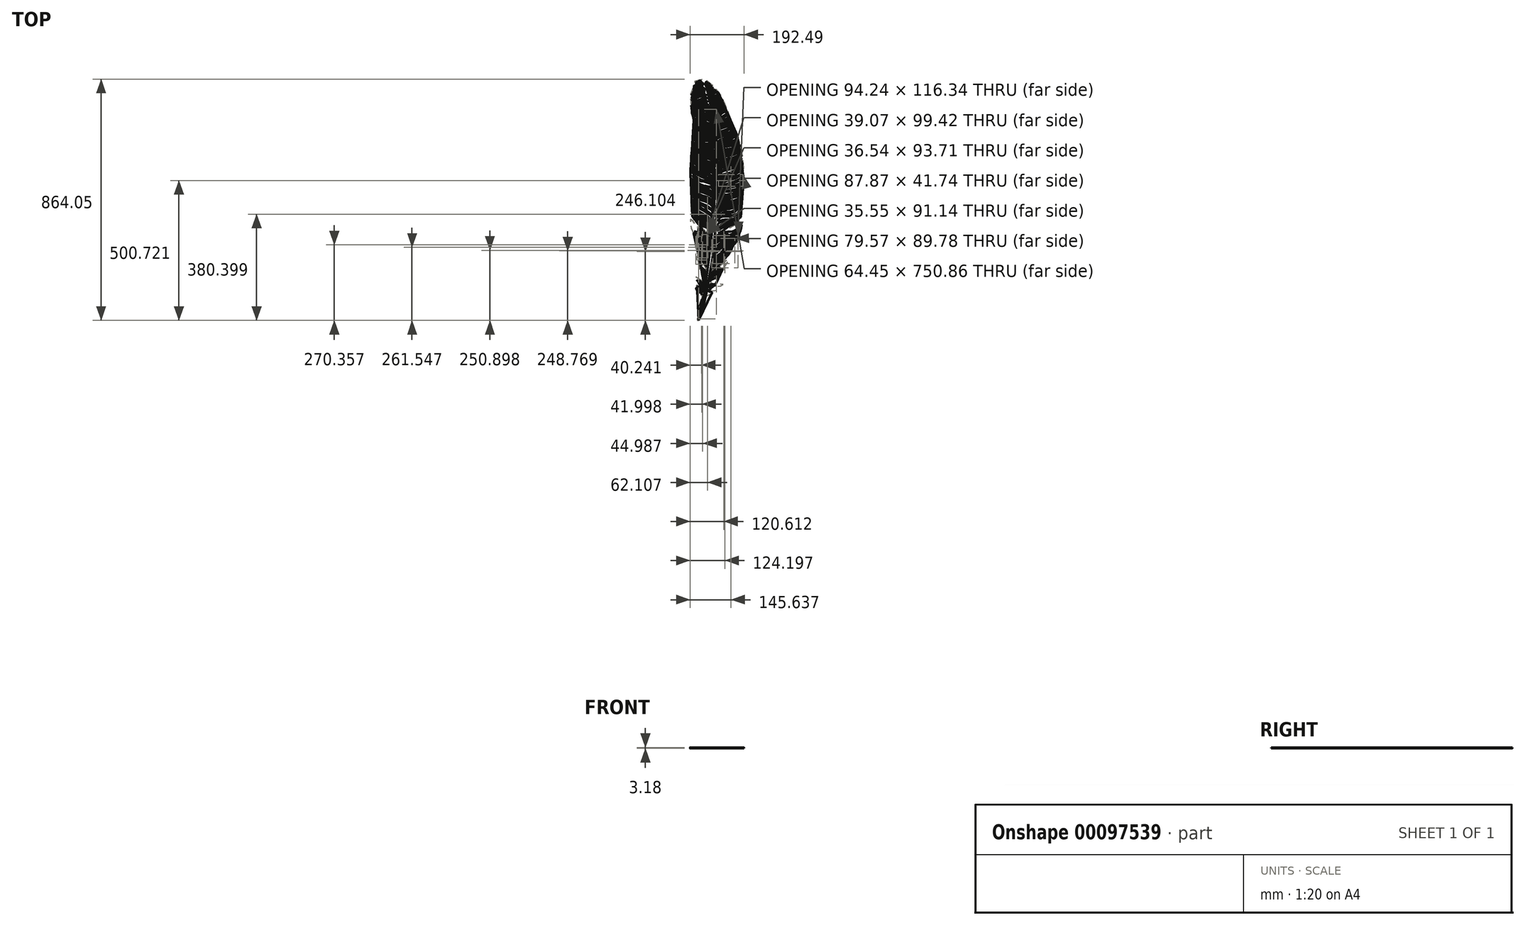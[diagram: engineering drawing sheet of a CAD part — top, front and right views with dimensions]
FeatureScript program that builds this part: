
annotation { "Feature Type Name" : "Feature", "Feature Type Description" : "" }
export const myFeature = defineFeature(function(context is Context, id is Id, definition is map)
    precondition{}
    {
        {
            var Q0;
            Q0=qCreatedBy(makeId("Top.planeOp"),FACE);
            var sketch = newSketch(context, id + "F0", { "sketchPlane" : qUnion([Q0])});
            skFitSpline(sketch, "E0", {"points": [v(-284.28, -414.74) * mm, v(-284.5, -404.7) * mm, v(-276.38, -375.66) * mm, v(-262.7, -314.79) * mm, v(-252.45, -245.37) * mm, v(-244.12, -173.4) * mm, v(-236.65, -109.74) * mm, v(-228.46, -20.33) * mm, v(-226.04, 99.02) * mm, v(-232.9, 203.45) * mm, v(-243.38, 304.25) * mm, v(-248.62, 349.81) * mm, v(-248.05, 351.8) * mm, v(-246.74, 348.7) * mm, v(-237.03, 303.26) * mm, v(-225.9, 221.44) * mm, v(-215.35, 72.9) * mm, v(-225.05, -107.86) * mm, v(-239.82, -235.78) * mm, v(-250.5, -289.17) * mm, v(-258.62, -340) * mm, v(-273.14, -389.13) * mm, v(-284.28, -414.74) * mm]});
            skFitSpline(sketch, "E1", {"points": [v(-284.28, -419.65) * mm, v(-282.38, -419.38) * mm, v(-274.71, -403.64) * mm, v(-261.46, -362.74) * mm, v(-255.63, -337.14) * mm, v(-254.22, -332.65) * mm, v(-249.64, -327.81) * mm, v(-238.34, -325.66) * mm, v(-232.96, -321.9) * mm, v(-241.03, -319.2) * mm, v(-250.18, -324.58) * mm, v(-251.26, -322.16) * mm, v(-246.74, -318.28) * mm, v(-242.56, -315.93) * mm, v(-229, -314.79) * mm, v(-220.02, -311.98) * mm, v(-223.55, -310.8) * mm, v(-240.85, -311.34) * mm, v(-248.54, -313.58) * mm, v(-249.4, -315.82) * mm, v(-250.25, -313.36) * mm, v(-246.74, -308.56) * mm, v(-243.63, -304.71) * mm, v(-234.44, -300.55) * mm, v(-221.41, -297.14) * mm, v(-216.4, -296.18) * mm, v(-189.8, -293.83) * mm, v(-190.55, -291.8) * mm, v(-196.32, -291.48) * mm, v(-219.28, -291.16) * mm, v(-225.9, -287.84) * mm, v(-230.8, -286.67) * mm, v(-241.06, -287.63) * mm, v(-243.73, -286.99) * mm, v(-242.66, -283.36) * mm, v(-232.73, -275.88) * mm, v(-227.07, -272.79) * mm, v(-222.7, -271.08) * mm, v(-213.62, -262.75) * mm, v(-201.65, -243.96) * mm, v(-193.54, -227.83) * mm, v(-177.73, -206.58) * mm, v(-177.3, -201.56) * mm, v(-176.99, -198.9) * mm, v(-179.87, -200.39) * mm, v(-181.26, -203.7) * mm, v(-192.58, -212.13) * mm, v(-197.28, -218.75) * mm, v(-207.2, -225.8) * mm, v(-221.95, -234.87) * mm, v(-233.8, -241.7) * mm, v(-238.82, -245.23) * mm, v(-237.64, -240.53) * mm, v(-231.24, -231.78) * mm, v(-222.8, -221.95) * mm, v(-212.23, -212.02) * mm, v(-199.41, -201.56) * mm, v(-190.01, -194.72) * mm, v(-179.98, -187.04) * mm, v(-171.65, -176.25) * mm, v(-166.2, -165.68) * mm, v(-154.67, -149.24) * mm, v(-151.03, -145.18) * mm, v(-143.88, -134.6) * mm, v(-138.33, -120.4) * mm, v(-138.75, -112.93) * mm, v(-136.4, -104.13) * mm, v(-134.48, -97.9) * mm, v(-132.08, -91.17) * mm, v(-130.48, -78.05) * mm, v(-134.32, -72.93) * mm, v(-140.08, -82.69) * mm, v(-147.28, -93.89) * mm, v(-161.53, -100.93) * mm, v(-185.05, -103) * mm, v(-204.89, -103.8) * mm, v(-213.37, -107.32) * mm, v(-211.6, -103.8) * mm, v(-200.73, -96.28) * mm, v(-180.57, -89.56) * mm, v(-172.89, -87.64) * mm, v(-165.05, -84.92) * mm, v(-144.72, -71.8) * mm, v(-132.72, -48.13) * mm, v(-130.64, -29.73) * mm, v(-128.72, -9.25) * mm, v(-127.92, 9.8) * mm, v(-127.12, 32.2) * mm, v(-123.76, 58.28) * mm, v(-121.68, 85.16) * mm, v(-122.32, 108.04) * mm, v(-123.28, 142.6) * mm, v(-126.48, 170.6) * mm, v(-130.48, 189.49) * mm, v(-137.68, 220.21) * mm, v(-148.73, 251.1) * mm, v(-164.73, 294.14) * mm, v(-180.25, 331.59) * mm, v(-195.13, 368.23) * mm, v(-200.4, 382.31) * mm, v(-214.49, 398.32) * mm, v(-238.97, 428.88) * mm, v(-252.73, 437.85) * mm, v(-264.1, 438.8) * mm, v(-267.77, 439.29) * mm, v(-270.5, 443.45) * mm, v(-288.74, 441.21) * mm, v(-298.82, 433.21) * mm, v(-300.9, 420.25) * mm, v(-305.22, 409.53) * mm, v(-312.73, 392.87) * mm, v(-313, 365.15) * mm, v(-308.96, 343.89) * mm, v(-308.15, 328.28) * mm, v(-306, 317.51) * mm, v(-300.62, 294.1) * mm, v(-299.81, 248.62) * mm, v(-305.73, 203.95) * mm, v(-309.77, 176.77) * mm, v(-311.38, 140.71) * mm, v(-311.38, 82.85) * mm, v(-308.96, 75.05) * mm, v(-311.92, 63.75) * mm, v(-310.85, 13.7) * mm, v(-311.92, -12.4) * mm, v(-310.04, -33.13) * mm, v(-299.27, -61.66) * mm, v(-276.38, -82.92) * mm, v(-246.74, -99.88) * mm, v(-240.6, -105) * mm, v(-238.38, -108.02) * mm, v(-240.08, -110.73) * mm, v(-245.85, -105.41) * mm, v(-266.67, -94.55) * mm, v(-284.28, -88.2) * mm, v(-298.46, -77.46) * mm, v(-304.23, -63.31) * mm, v(-308.76, -57.43) * mm, v(-313.17, -54.94) * mm, v(-312.38, -60.14) * mm, v(-311.13, -85.94) * mm, v(-304.23, -102.91) * mm, v(-294.84, -130.86) * mm, v(-290.31, -178.04) * mm, v(-256.14, -231) * mm, v(-256.03, -234.85) * mm, v(-257.27, -238.36) * mm, v(-274.59, -218.44) * mm, v(-286.13, -197.05) * mm, v(-288.95, -195.92) * mm, v(-288.05, -198.52) * mm, v(-285.45, -211.88) * mm, v(-274.59, -255.9) * mm, v(-265.3, -276.71) * mm, v(-261.12, -280.9) * mm, v(-262.7, -290.63) * mm, v(-266.78, -283.84) * mm, v(-280.8, -273.2) * mm, v(-295.3, -262.68) * mm, v(-297.21, -262.68) * mm, v(-296.88, -265.17) * mm, v(-293.48, -272.75) * mm, v(-287.14, -278.18) * mm, v(-277.41, -297.42) * mm, v(-266.67, -308.5) * mm, v(-266.78, -312.47) * mm, v(-268.93, -314.79) * mm, v(-280.7, -302.73) * mm, v(-288.95, -295.94) * mm, v(-283.07, -308.96) * mm, v(-270.85, -319.14) * mm, v(-272.32, -320.16) * mm, v(-288.5, -307.03) * mm, v(-292.35, -302.84) * mm, v(-291.9, -310.09) * mm, v(-284.28, -315.63) * mm, v(-275.5, -321.85) * mm, v(-272.1, -328.76) * mm, v(-272.32, -342.1) * mm, v(-281.94, -377.75) * mm, v(-288.05, -402.75) * mm, v(-288.28, -417) * mm, v(-287.37, -419.5) * mm, v(-284.28, -419.65) * mm]});
            skFitSpline(sketch, "E2", {"points": [v(-283.14, 436.73) * mm, v(-280.72, 434.91) * mm, v(-274.71, 435.72) * mm, v(-277.5, 438.74) * mm, v(-281.93, 439.15) * mm, v(-283.14, 436.73) * mm]});
            skFitSpline(sketch, "E3", {"points": [v(-266.2, 424.83) * mm, v(-270.04, 426.04) * mm, v(-279.1, 425.84) * mm, v(-291, 426.04) * mm, v(-292.82, 430.28) * mm, v(-290.8, 431.69) * mm, v(-291.2, 434.5) * mm, v(-288.58, 433.1) * mm, v(-281.93, 431.48) * mm, v(-271.85, 431.08) * mm, v(-266.2, 428.05) * mm, v(-266.2, 424.83) * mm]});
            skFitSpline(sketch, "E4", {"points": [v(-266.58, 419.95) * mm, v(-272.15, 418.87) * mm, v(-282.92, 416.54) * mm, v(-285.08, 415.1) * mm, v(-292.98, 415.64) * mm, v(-296.4, 420.31) * mm, v(-296.75, 422.3) * mm, v(-293.16, 421.21) * mm, v(-286.7, 421.93) * mm, v(-279.69, 421.75) * mm, v(-272.86, 422.65) * mm, v(-269.81, 420.31) * mm, v(-266.58, 419.95) * mm]});
            skFitSpline(sketch, "E5", {"points": [v(-257.2, 434.22) * mm, v(-258.33, 429.92) * mm, v(-261.95, 425.4) * mm, v(-260.14, 424.49) * mm, v(-256.74, 428.56) * mm, v(-252.9, 431.28) * mm, v(-254.03, 434) * mm, v(-257.2, 434.22) * mm]});
            skFitSpline(sketch, "E6", {"points": [v(-257.42, 418.6) * mm, v(-255.16, 423.8) * mm, v(-248.37, 429.47) * mm, v(-246.33, 428.79) * mm, v(-243.85, 425.4) * mm, v(-247.47, 424.49) * mm, v(-256.07, 415.66) * mm, v(-257.42, 418.6) * mm]});
            skFitSpline(sketch, "E7", {"points": [v(-266.7, 413.85) * mm, v(-273.49, 412.05) * mm, v(-280.73, 408.65) * mm, v(-291.14, 407.07) * mm, v(-302.23, 405.94) * mm, v(-300.87, 409.79) * mm, v(-296.8, 412.5) * mm, v(-291.82, 410.01) * mm, v(-280.73, 412.05) * mm, v(-273.04, 414.53) * mm, v(-266.7, 413.85) * mm]});
            skFitSpline(sketch, "E8", {"points": [v(-237.5, 417.47) * mm, v(-241.13, 416.34) * mm, v(-247.47, 410.46) * mm, v(-253.8, 405.93) * mm, v(-256.74, 405.25) * mm, v(-254.7, 409.33) * mm, v(-249.28, 415.89) * mm, v(-244.98, 419.5) * mm, v(-238.64, 419.96) * mm, v(-237.5, 417.47) * mm]});
            skFitSpline(sketch, "E9", {"points": [v(-262.85, 406.84) * mm, v(-263.76, 405.03) * mm, v(-271.45, 403.45) * mm, v(-281.18, 401.86) * mm, v(-289.33, 400.5) * mm, v(-297.25, 396.2) * mm, v(-304.5, 397.12) * mm, v(-300.64, 400.5) * mm, v(-291.14, 402.54) * mm, v(-278.02, 405.7) * mm, v(-270.32, 409.1) * mm, v(-263.99, 409.78) * mm, v(-262.85, 406.84) * mm]});
            skFitSpline(sketch, "E10", {"points": [v(-260.6, 397.79) * mm, v(-262.63, 400.73) * mm, v(-273.72, 399.37) * mm, v(-286.61, 396.2) * mm, v(-293.63, 393.95) * mm, v(-305.62, 390.78) * mm, v(-309.02, 390.55) * mm, v(-308.34, 386.48) * mm, v(-300.64, 387.84) * mm, v(-286.39, 392.81) * mm, v(-273.26, 397.34) * mm, v(-260.6, 397.79) * mm]});
            skFitSpline(sketch, "E11", {"points": [v(-182.7, -107.46) * mm, v(-201.65, -107.7) * mm, v(-214.49, -112.97) * mm, v(-221.95, -122.32) * mm, v(-221.95, -129.27) * mm, v(-219.62, -125.67) * mm, v(-207.2, -117.52) * mm, v(-190.61, -111.77) * mm, v(-182.7, -107.46) * mm]});
            skFitSpline(sketch, "E12", {"points": [v(-221.78, -141.74) * mm, v(-223.94, -145.1) * mm, v(-225.37, -142.22) * mm, v(-223.7, -135.26) * mm, v(-213.39, -126.15) * mm, v(-193.97, -117.53) * mm, v(-177.9, -111.06) * mm, v(-198.52, -122.32) * mm, v(-216.98, -136.94) * mm, v(-221.78, -141.74) * mm]});
            skFitSpline(sketch, "E13", {"points": [v(-264.68, -304.71) * mm, v(-271.8, -297.42) * mm, v(-279.34, -283.64) * mm, v(-281.63, -278.26) * mm, v(-279.88, -278.12) * mm, v(-273.15, -285.26) * mm, v(-267.23, -294) * mm, v(-263.74, -297.42) * mm, v(-264.68, -300.06) * mm, v(-264.68, -304.71) * mm]});
            skFitSpline(sketch, "E14", {"points": [v(-223.5, -293.07) * mm, v(-230.64, -290.78) * mm, v(-239.92, -290.64) * mm, v(-245.57, -293.6) * mm, v(-246.92, -296.3) * mm, v(-248.4, -300.73) * mm, v(-242.07, -298.45) * mm, v(-234.27, -296.56) * mm, v(-226.6, -294.41) * mm, v(-223.5, -293.07) * mm]});
            skFitSpline(sketch, "E15", {"points": [v(-205.8, -244.3) * mm, v(-215.65, -252.7) * mm, v(-226.62, -259.68) * mm, v(-235.75, -266.1) * mm, v(-242.66, -273.22) * mm, v(-244.58, -278.36) * mm, v(-237.17, -274.37) * mm, v(-225.77, -268.1) * mm, v(-213.8, -256.55) * mm, v(-205.8, -244.3) * mm]});
            skFitSpline(sketch, "E16", {"points": [v(-258.7, -269.09) * mm, v(-258.13, -275.08) * mm, v(-261.7, -272.65) * mm, v(-265.11, -265.52) * mm, v(-266.97, -260.4) * mm, v(-262.26, -264.67) * mm, v(-258.7, -269.09) * mm]});
            skFitSpline(sketch, "E17", {"points": [v(-258.98, -262.39) * mm, v(-264.26, -256.68) * mm, v(-270.67, -245.56) * mm, v(-271.38, -242.57) * mm, v(-264.54, -249.13) * mm, v(-258.98, -254.7) * mm, v(-258.98, -262.39) * mm]});
            skFitSpline(sketch, "E18", {"points": [v(-243.3, -266.95) * mm, v(-234.9, -260.25) * mm, v(-222.49, -252.7) * mm, v(-214.93, -247.14) * mm, v(-209.37, -241.87) * mm, v(-206.67, -236.3) * mm, v(-213.08, -240.01) * mm, v(-226.62, -249.7) * mm, v(-235.18, -256.55) * mm, v(-240.3, -261.4) * mm, v(-243.3, -266.95) * mm]});
            skFitSpline(sketch, "E19", {"points": [v(-239.6, -250.99) * mm, v(-231.18, -243.86) * mm, v(-218.64, -236.88) * mm, v(-207.52, -229.18) * mm, v(-216.79, -238.87) * mm, v(-226.2, -244.15) * mm, v(-239.88, -255.83) * mm, v(-240.74, -254.12) * mm, v(-239.6, -250.99) * mm]});
            skFitSpline(sketch, "E20", {"points": [v(-258.23, -250.25) * mm, v(-264.88, -243.78) * mm, v(-270.98, -236.06) * mm, v(-273.5, -230.3) * mm, v(-266.85, -236.06) * mm, v(-258.95, -243.6) * mm, v(-258.23, -250.25) * mm]});
            skFitSpline(sketch, "E21", {"points": [v(-242.79, -135.26) * mm, v(-250.26, -119.72) * mm, v(-263.3, -106.9) * mm, v(-283.16, -96.01) * mm, v(-285.3, -92.8) * mm, v(-274.4, -96.87) * mm, v(-257.53, -104.56) * mm, v(-242.79, -114.39) * mm, v(-240.01, -118.02) * mm, v(-241.93, -122.5) * mm, v(-242.79, -135.26) * mm]});
            skFitSpline(sketch, "E22", {"points": [v(-237.08, -231.78) * mm, v(-235.94, -225.99) * mm, v(-231.24, -218.76) * mm, v(-213.37, -204.1) * mm, v(-200.73, -192.31) * mm, v(-188, -180.9) * mm, v(-181.52, -171.2) * mm, v(-174.29, -159.78) * mm, v(-160.4, -144.37) * mm, v(-148.41, -127.82) * mm, v(-141.94, -114.39) * mm, v(-142.32, -122.32) * mm, v(-152.03, -140.18) * mm, v(-163.63, -155.79) * mm, v(-174.48, -174.62) * mm, v(-183.42, -185.47) * mm, v(-192.56, -191.55) * mm, v(-203.78, -200.69) * mm, v(-224.9, -219.14) * mm, v(-237.08, -231.78) * mm]});
            skFitSpline(sketch, "E23", {"points": [v(-233.33, -215.83) * mm, v(-234.01, -212.02) * mm, v(-231.24, -205.42) * mm, v(-222.8, -196.6) * mm, v(-212.23, -189.58) * mm, v(-197.28, -175.78) * mm, v(-186.5, -159.72) * mm, v(-177.67, -149.24) * mm, v(-161.15, -135.74) * mm, v(-151.03, -122.61) * mm, v(-157.07, -135.28) * mm, v(-170.65, -149.24) * mm, v(-181.51, -164.47) * mm, v(-188.53, -174.88) * mm, v(-202.1, -188.9) * mm, v(-222.8, -206.1) * mm, v(-233.33, -215.83) * mm]});
            skFitSpline(sketch, "E24", {"points": [v(-254.39, -218.52) * mm, v(-252.9, -223) * mm, v(-254.39, -227.7) * mm, v(-264, -215.1) * mm, v(-276.17, -197.8) * mm, v(-284.5, -180.07) * mm, v(-287.28, -159.78) * mm, v(-288.99, -140.13) * mm, v(-293.69, -119.84) * mm, v(-299.67, -106.38) * mm, v(-290.48, -121.12) * mm, v(-280.44, -140.35) * mm, v(-276.39, -167.9) * mm, v(-276.17, -181.78) * mm, v(-261.65, -208.91) * mm, v(-254.39, -218.52) * mm]});
            skFitSpline(sketch, "E25", {"points": [v(-254.39, -201.13) * mm, v(-252.43, -204.1) * mm, v(-252.6, -213) * mm, v(-261.65, -200.28) * mm, v(-267.35, -191.12) * mm, v(-270.23, -175.18) * mm, v(-272.6, -154.16) * mm, v(-276.33, -138.74) * mm, v(-282.44, -127.2) * mm, v(-290.74, -113.3) * mm, v(-296.5, -100.25) * mm, v(-287.35, -112.97) * mm, v(-276.16, -128.56) * mm, v(-266.33, -148.74) * mm, v(-266.33, -161.45) * mm, v(-265.15, -177.22) * mm, v(-260.4, -191.3) * mm, v(-254.39, -201.13) * mm]});
            skFitSpline(sketch, "E26", {"points": [v(-250.9, -196.2) * mm, v(-257, -189.09) * mm, v(-260.57, -174.85) * mm, v(-261.59, -161.45) * mm, v(-262.6, -145.52) * mm, v(-272.1, -126.87) * mm, v(-282.78, -111.95) * mm, v(-288.2, -102.12) * mm, v(-281.08, -109.07) * mm, v(-267.18, -124.33) * mm, v(-257.35, -141.28) * mm, v(-254.63, -161.8) * mm, v(-253.96, -177.22) * mm, v(-250.74, -181.12) * mm, v(-250.23, -186.38) * mm, v(-250.9, -196.2) * mm]});
            skFitSpline(sketch, "E27", {"points": [v(-248.4, -170.83) * mm, v(-250.95, -151.53) * mm, v(-256.54, -132.22) * mm, v(-266.44, -118.25) * mm, v(-281.08, -102.75) * mm, v(-266.19, -109.07) * mm, v(-253.74, -123.08) * mm, v(-246.63, -140.86) * mm, v(-245.18, -149.47) * mm, v(-245.18, -166.1) * mm, v(-248.4, -170.83) * mm]});
            skFitSpline(sketch, "E28", {"points": [v(-226.9, -162.42) * mm, v(-227.97, -158.38) * mm, v(-224.74, -148.16) * mm, v(-207.25, -133.9) * mm, v(-194.6, -123.67) * mm, v(-178.72, -116.41) * mm, v(-153.7, -105.92) * mm, v(-163.12, -113.18) * mm, v(-179.53, -123.14) * mm, v(-194.06, -131.2) * mm, v(-205.64, -143.05) * mm, v(-218.82, -155.16) * mm, v(-226.9, -162.42) * mm]});
            skFitSpline(sketch, "E29", {"points": [v(-227.35, -182.18) * mm, v(-229.16, -179.24) * mm, v(-226.45, -168.6) * mm, v(-210.38, -152.08) * mm, v(-198.39, -139.87) * mm, v(-188.2, -132.17) * mm, v(-174.85, -124.26) * mm, v(-154.26, -112.72) * mm, v(-145.66, -105.25) * mm, v(-152, -115.89) * mm, v(-173.95, -129.91) * mm, v(-192.96, -145.07) * mm, v(-206.76, -160.23) * mm, v(-221.92, -173.58) * mm, v(-227.35, -182.18) * mm]});
            skFitSpline(sketch, "E30", {"points": [v(-231.24, -199.53) * mm, v(-232.35, -195.4) * mm, v(-227.92, -187.62) * mm, v(-215.67, -172.94) * mm, v(-202.7, -160.93) * mm, v(-191.07, -148.34) * mm, v(-175.49, -134.8) * mm, v(-157.39, -123.3) * mm, v(-166.62, -136.84) * mm, v(-184, -150.02) * mm, v(-196.23, -167.28) * mm, v(-208.58, -182.26) * mm, v(-220.92, -190.65) * mm, v(-231.24, -199.53) * mm]});
            skFitSpline(sketch, "E31", {"points": [v(-216.4, -96.28) * mm, v(-217.48, -96.28) * mm, v(-214.96, -90.35) * mm, v(-204.89, -83.7) * mm, v(-198.2, -81.7) * mm, v(-189.37, -79.9) * mm, v(-162.71, -70.72) * mm, v(-143.61, -61.18) * mm, v(-154.96, -73.24) * mm, v(-173.34, -80.45) * mm, v(-191.53, -86.03) * mm, v(-204.89, -90.71) * mm, v(-213.39, -96.28) * mm, v(-216.4, -96.28) * mm]});
            skFitSpline(sketch, "E32", {"points": [v(-239.1, -99.9) * mm, v(-247.92, -91.97) * mm, v(-263.42, -84.77) * mm, v(-278.19, -76.85) * mm, v(-286.3, -70.36) * mm, v(-293.86, -59.56) * mm, v(-298.73, -49.11) * mm, v(-288.46, -61.9) * mm, v(-278.73, -68.74) * mm, v(-261.62, -76.13) * mm, v(-249.36, -82.6) * mm, v(-242.52, -89.1) * mm, v(-239.1, -99.9) * mm]});
            skFitSpline(sketch, "E33", {"points": [v(-218.56, -87.65) * mm, v(-217.66, -81.35) * mm, v(-212.61, -72.7) * mm, v(-200.9, -66.4) * mm, v(-179.1, -62.62) * mm, v(-159.65, -61.36) * mm, v(-146.32, -57.04) * mm, v(-157.49, -64.6) * mm, v(-181.45, -71.44) * mm, v(-187.75, -72.16) * mm, v(-193.52, -74.5) * mm, v(-202.7, -77.39) * mm, v(-218.56, -87.65) * mm]});
            skFitSpline(sketch, "E34", {"points": [v(-237.9, -85.23) * mm, v(-245.43, -79.78) * mm, v(-256.35, -74) * mm, v(-271.27, -65.82) * mm, v(-281.7, -59.88) * mm, v(-292.94, -49.94) * mm, v(-300.49, -40.47) * mm, v(-303.86, -31) * mm, v(-304.98, -23.94) * mm, v(-298.08, -33.9) * mm, v(-282.19, -50.9) * mm, v(-268.55, -61.65) * mm, v(-247.04, -70.8) * mm, v(-238.7, -75.6) * mm, v(-236.77, -81.22) * mm, v(-237.9, -85.23) * mm]});
            skFitSpline(sketch, "E35", {"points": [v(-230.83, 412.33) * mm, v(-233.9, 412.69) * mm, v(-238.22, 411.43) * mm, v(-247.04, 403.86) * mm, v(-253.17, 397.74) * mm, v(-250.1, 397.92) * mm, v(-244.89, 399.72) * mm, v(-237.32, 405.66) * mm, v(-230.83, 412.33) * mm]});
            skFitSpline(sketch, "E36", {"points": [v(-257.68, 385.5) * mm, v(-259.3, 389.46) * mm, v(-263.98, 391.98) * mm, v(-275.15, 392.16) * mm, v(-286.32, 388.01) * mm, v(-294.25, 384.6) * mm, v(-305.6, 382.61) * mm, v(-309.02, 379.91) * mm, v(-307.4, 376.13) * mm, v(-300.2, 376.67) * mm, v(-287.4, 382.97) * mm, v(-277.13, 387.65) * mm, v(-264.7, 387.65) * mm, v(-257.68, 385.5) * mm]});
            skFitSpline(sketch, "E37", {"points": [v(-237, -67.6) * mm, v(-236.42, -71.62) * mm, v(-243.48, -67.04) * mm, v(-258.37, -59.02) * mm, v(-273.64, -50.82) * mm, v(-284.52, -42.42) * mm, v(-293.68, -32.31) * mm, v(-301.13, -21.63) * mm, v(-302.84, -15.52) * mm, v(-306.85, -8.84) * mm, v(-306.66, -4.64) * mm, v(-304.56, -8.08) * mm, v(-298.26, -16.66) * mm, v(-286.24, -33.46) * mm, v(-270.59, -44.33) * mm, v(-258.37, -50.06) * mm, v(-247.11, -56.35) * mm, v(-240.43, -61.89) * mm, v(-238.7, -66.66) * mm, v(-237, -67.6) * mm]});
            skFitSpline(sketch, "E38", {"points": [v(-213.4, -66.26) * mm, v(-212.95, -59.13) * mm, v(-208.37, -52.86) * mm, v(-196.93, -47.08) * mm, v(-183.72, -47.27) * mm, v(-156.68, -46.3) * mm, v(-142.23, -38.73) * mm, v(-133.81, -31.5) * mm, v(-135.42, -36.1) * mm, v(-137.87, -43.82) * mm, v(-147.07, -52.3) * mm, v(-166.86, -57.67) * mm, v(-185.03, -58.85) * mm, v(-198.57, -60.06) * mm, v(-207.64, -63.97) * mm, v(-213.4, -67.64) * mm, v(-213.4, -66.26) * mm]});
            skFitSpline(sketch, "E39", {"points": [v(-235.7, -60.63) * mm, v(-234.96, -52.86) * mm, v(-239.79, -45) * mm, v(-256.9, -32.46) * mm, v(-277.8, -20.05) * mm, v(-291.66, -10.03) * mm, v(-303.58, 5.5) * mm, v(-304.7, 9.57) * mm, v(-305.18, 2.37) * mm, v(-301.55, -5.18) * mm, v(-295.88, -14.35) * mm, v(-284.82, -27.2) * mm, v(-269.96, -37.8) * mm, v(-247.17, -51.2) * mm, v(-235.7, -60.63) * mm]});
            skFitSpline(sketch, "E40", {"points": [v(-234.55, -42.54) * mm, v(-249.68, -30.17) * mm, v(-264.2, -22.18) * mm, v(-280.72, -11.8) * mm, v(-294.23, 0) * mm, v(-301.86, 12.64) * mm, v(-295.65, 6.48) * mm, v(-276, -5.64) * mm, v(-250.06, -18.54) * mm, v(-234.56, -29.07) * mm, v(-235.53, -37.57) * mm, v(-234.55, -42.54) * mm]});
            skFitSpline(sketch, "E41", {"points": [v(-233.42, -22.2) * mm, v(-250.48, -12.02) * mm, v(-271.74, -1.75) * mm, v(-292.82, 11.59) * mm, v(-303.13, 21.19) * mm, v(-304.88, 28.61) * mm, v(-300.55, 25.2) * mm, v(-285.8, 14.88) * mm, v(-268.4, 8.25) * mm, v(-249.7, 1.46) * mm, v(-238.18, -7.33) * mm, v(-232.77, -14.89) * mm, v(-233.42, -22.2) * mm]});
            skFitSpline(sketch, "E42", {"points": [v(-233.22, -5.38) * mm, v(-241.18, 0) * mm, v(-252.45, 7.56) * mm, v(-270.17, 14.08) * mm, v(-289.89, 22.44) * mm, v(-303.49, 34.04) * mm, v(-307.72, 43.06) * mm, v(-299.98, 36.81) * mm, v(-277.34, 23.93) * mm, v(-254.84, 16.19) * mm, v(-243.04, 11.05) * mm, v(-233.54, 2.5) * mm, v(-233.68, 0) * mm, v(-233.22, -5.38) * mm]});
            skFitSpline(sketch, "E43", {"points": [v(-231.24, 7.35) * mm, v(-242.54, 16.43) * mm, v(-263.71, 25.61) * mm, v(-280.03, 31.8) * mm, v(-299.77, 42.23) * mm, v(-308.01, 54.78) * mm, v(-307.2, 58.05) * mm, v(-304.38, 53.05) * mm, v(-282.72, 41.9) * mm, v(-252.2, 32.2) * mm, v(-237.38, 23) * mm, v(-230.4, 15.9) * mm, v(-230.94, 11) * mm, v(-231.24, 7.35) * mm]});
            skFitSpline(sketch, "E44", {"points": [v(-230.22, 21.16) * mm, v(-239.35, 30.77) * mm, v(-266.22, 40.98) * mm, v(-289.15, 48.77) * mm, v(-300.68, 56.76) * mm, v(-306.73, 64.08) * mm, v(-306.56, 72.22) * mm, v(-305.1, 69.96) * mm, v(-293.4, 60.67) * mm, v(-278.36, 50.32) * mm, v(-259.84, 44.83) * mm, v(-243.07, 39.4) * mm, v(-232.85, 33.01) * mm, v(-230.53, 28.4) * mm, v(-230.22, 21.16) * mm]});
            skFitSpline(sketch, "E45", {"points": [v(-231.35, 38.27) * mm, v(-239.72, 45.07) * mm, v(-258.72, 49.66) * mm, v(-278.23, 56.07) * mm, v(-297.03, 68.97) * mm, v(-301.41, 72.87) * mm, v(-304.52, 78.7) * mm, v(-306.72, 86.82) * mm, v(-300.5, 80.29) * mm, v(-279.26, 63.4) * mm, v(-260.62, 56.3) * mm, v(-244.02, 56.66) * mm, v(-237.15, 53.4) * mm, v(-232.01, 46.68) * mm, v(-230.79, 43.97) * mm, v(-231.35, 38.27) * mm]});
            skFitSpline(sketch, "E46", {"points": [v(-229.05, 52.57) * mm, v(-234.16, 58) * mm, v(-242.1, 59.62) * mm, v(-258.57, 61.33) * mm, v(-273.88, 65.95) * mm, v(-286.16, 73.87) * mm, v(-297.96, 85.58) * mm, v(-303.78, 94.78) * mm, v(-304.36, 101.42) * mm, v(-302.81, 97.39) * mm, v(-289.93, 85.87) * mm, v(-276.03, 78.7) * mm, v(-265.22, 78.17) * mm, v(-254.23, 74.1) * mm, v(-243.6, 69.74) * mm, v(-231.56, 61.36) * mm, v(-229.05, 52.57) * mm]});
            skFitSpline(sketch, "E47", {"points": [v(-229.67, 65.61) * mm, v(-240.84, 73.88) * mm, v(-256.58, 79.99) * mm, v(-277.34, 84.63) * mm, v(-287, 90.15) * mm, v(-298.13, 99.37) * mm, v(-304.7, 110.75) * mm, v(-306.6, 114.51) * mm, v(-295.21, 106.54) * mm, v(-271.45, 93.36) * mm, v(-246.63, 83.24) * mm, v(-235.44, 77.22) * mm, v(-230, 72.7) * mm, v(-229.87, 69) * mm, v(-229.67, 65.61) * mm]});
            skFitSpline(sketch, "E48", {"points": [v(-229.4, 79.36) * mm, v(-231.6, 80.9) * mm, v(-245.72, 89.22) * mm, v(-264.04, 96.45) * mm, v(-286.6, 107.56) * mm, v(-299.44, 115.55) * mm, v(-306.19, 124.55) * mm, v(-306.6, 132.77) * mm, v(-304.4, 129.78) * mm, v(-284.86, 116.15) * mm, v(-264.68, 104.21) * mm, v(-246.7, 98.95) * mm, v(-232.54, 90.15) * mm, v(-228.74, 86.32) * mm, v(-229.4, 79.36) * mm]});
            skFitSpline(sketch, "E49", {"points": [v(-230.06, 95.75) * mm, v(-230.49, 104.7) * mm, v(-241.78, 111.94) * mm, v(-257.93, 117.71) * mm, v(-274.22, 124.85) * mm, v(-287.95, 132.74) * mm, v(-298.79, 141.45) * mm, v(-306.8, 149.36) * mm, v(-306.54, 142.05) * mm, v(-296.15, 129.08) * mm, v(-265.97, 111.83) * mm, v(-243.65, 103.15) * mm, v(-230.06, 95.75) * mm]});
            skFitSpline(sketch, "E50", {"points": [v(-230.59, 111.91) * mm, v(-232.74, 119.05) * mm, v(-239.43, 125.26) * mm, v(-271.63, 137.31) * mm, v(-283.02, 141.14) * mm, v(-295.3, 148.59) * mm, v(-301.92, 155.73) * mm, v(-306.58, 160.35) * mm, v(-304.42, 153.21) * mm, v(-293.35, 141.61) * mm, v(-278.55, 133.18) * mm, v(-262.4, 126.48) * mm, v(-243.49, 118.08) * mm, v(-230.59, 111.91) * mm]});
            skFitSpline(sketch, "E51", {"points": [v(-231.3, 125.6) * mm, v(-231.02, 133.11) * mm, v(-238.1, 139.9) * mm, v(-249.34, 143.86) * mm, v(-267.53, 148.4) * mm, v(-282.45, 153.2) * mm, v(-293.6, 161.3) * mm, v(-302.42, 169.26) * mm, v(-304.2, 170.3) * mm, v(-304, 166.36) * mm, v(-299.63, 159.09) * mm, v(-288.9, 149.55) * mm, v(-269.82, 142.61) * mm, v(-251.55, 136.59) * mm, v(-238.66, 130.95) * mm, v(-231.3, 125.6) * mm]});
            skFitSpline(sketch, "E52", {"points": [v(-240.2, 156.2) * mm, v(-234.96, 152.15) * mm, v(-233.3, 149) * mm, v(-232.62, 143.86) * mm, v(-241.2, 147.04) * mm, v(-256.13, 150.7) * mm, v(-268.85, 153.85) * mm, v(-283.16, 159.46) * mm, v(-294.13, 167.16) * mm, v(-300.23, 173.12) * mm, v(-302.62, 176.82) * mm, v(-302.28, 182.66) * mm, v(-299.23, 179.12) * mm, v(-287, 168.32) * mm, v(-269.75, 160.75) * mm, v(-252.1, 159.25) * mm, v(-240.2, 156.2) * mm]});
            skFitSpline(sketch, "E53", {"points": [v(-233, 158.7) * mm, v(-233.25, 163.72) * mm, v(-241.57, 171.1) * mm, v(-255.85, 173.76) * mm, v(-271.76, 174.6) * mm, v(-280.52, 177.71) * mm, v(-289.83, 182.26) * mm, v(-301.4, 191.16) * mm, v(-298.67, 186.07) * mm, v(-288.73, 175.33) * mm, v(-270.47, 166.5) * mm, v(-255.87, 165.38) * mm, v(-244.1, 163.7) * mm, v(-235.68, 159.95) * mm, v(-233, 158.7) * mm]});
            skFitSpline(sketch, "E54", {"points": [v(-234.88, 172.9) * mm, v(-235.3, 177.79) * mm, v(-240.57, 183.01) * mm, v(-250.48, 185) * mm, v(-268.79, 185.99) * mm, v(-282.16, 189.42) * mm, v(-295.4, 194.61) * mm, v(-302.42, 199.3) * mm, v(-301.06, 195.56) * mm, v(-294.37, 190.42) * mm, v(-281.27, 182.19) * mm, v(-273.16, 179.4) * mm, v(-258.97, 178.93) * mm, v(-248.02, 178.6) * mm, v(-237.53, 176.03) * mm, v(-234.88, 172.9) * mm]});
            skFitSpline(sketch, "E55", {"points": [v(-235.63, 187.07) * mm, v(-237.3, 193.57) * mm, v(-246.68, 197.58) * mm, v(-262.01, 198.14) * mm, v(-275.46, 198.47) * mm, v(-285.4, 199.7) * mm, v(-294.37, 205.32) * mm, v(-299.7, 209.65) * mm, v(-299.53, 206.2) * mm, v(-289.83, 197.1) * mm, v(-277.1, 192.96) * mm, v(-266.2, 190.42) * mm, v(-254.5, 191.66) * mm, v(-243.87, 190.42) * mm, v(-235.63, 187.07) * mm]});
            skFitSpline(sketch, "E56", {"points": [v(-299.42, 219.52) * mm, v(-297.76, 213.07) * mm, v(-291.7, 208) * mm, v(-283.94, 204.8) * mm, v(-275.46, 203.54) * mm, v(-262.01, 203.66) * mm, v(-249.34, 203.3) * mm, v(-241.2, 200.9) * mm, v(-236.47, 198.47) * mm, v(-236.48, 205.19) * mm, v(-239.41, 207.47) * mm, v(-253.86, 208.3) * mm, v(-270.27, 208.88) * mm, v(-282.16, 210.23) * mm, v(-292.04, 213.65) * mm, v(-299.42, 219.52) * mm]});
            skFitSpline(sketch, "E57", {"points": [v(-296.48, 226.05) * mm, v(-291.74, 219.53) * mm, v(-280.33, 214.6) * mm, v(-264.11, 213.08) * mm, v(-246.74, 212.86) * mm, v(-237.88, 212.89) * mm, v(-238.55, 217.61) * mm, v(-242.93, 219.28) * mm, v(-244.46, 221.23) * mm, v(-258.99, 222.38) * mm, v(-273.2, 219.97) * mm, v(-286.75, 220.84) * mm, v(-296.48, 226.05) * mm]});
            skFitSpline(sketch, "E58", {"points": [v(-297.14, 235.9) * mm, v(-293.48, 230.64) * mm, v(-287.2, 226.66) * mm, v(-269.1, 226.35) * mm, v(-252.44, 227.02) * mm, v(-244.1, 225.99) * mm, v(-239.16, 224.1) * mm, v(-240.15, 230.14) * mm, v(-246.85, 233.53) * mm, v(-258.88, 235.34) * mm, v(-273.2, 233.9) * mm, v(-285.96, 233.56) * mm, v(-292.1, 236.07) * mm, v(-297.14, 235.9) * mm]});
            skFitSpline(sketch, "E59", {"points": [v(-240.75, 239.07) * mm, v(-247.85, 242.67) * mm, v(-258.88, 243.47) * mm, v(-275.75, 243.4) * mm, v(-286.54, 245.53) * mm, v(-292.88, 250.63) * mm, v(-296.3, 253.46) * mm, v(-296.19, 243.03) * mm, v(-290.38, 240.4) * mm, v(-280.6, 238.39) * mm, v(-264.4, 238.95) * mm, v(-252.44, 238.85) * mm, v(-245.84, 238.74) * mm, v(-240.75, 239.07) * mm]});
            skFitSpline(sketch, "E60", {"points": [v(-293.74, 259.55) * mm, v(-289.3, 254.52) * mm, v(-282.18, 250.27) * mm, v(-273.9, 248.93) * mm, v(-259.08, 249.18) * mm, v(-247.4, 248.54) * mm, v(-240.94, 246.94) * mm, v(-242.5, 253.06) * mm, v(-247.68, 255.95) * mm, v(-255.15, 256.23) * mm, v(-266.31, 255.04) * mm, v(-279.86, 254.47) * mm, v(-288.12, 257.41) * mm, v(-293.74, 259.55) * mm]});
            skFitSpline(sketch, "E61", {"points": [v(-295.03, 267.08) * mm, v(-292.32, 265.14) * mm, v(-290.59, 263.48) * mm, v(-285.2, 260.9) * mm, v(-266.68, 260.53) * mm, v(-254.9, 262.6) * mm, v(-246.87, 261.45) * mm, v(-242.56, 258.68) * mm, v(-244.9, 263.13) * mm, v(-251, 268.05) * mm, v(-262.2, 267.35) * mm, v(-269.27, 265.98) * mm, v(-283.31, 265.15) * mm, v(-291, 266.58) * mm, v(-295.03, 267.08) * mm]});
            skFitSpline(sketch, "E62", {"points": [v(-293.87, 274.3) * mm, v(-283.98, 273.8) * mm, v(-270.36, 276.1) * mm, v(-259.56, 277.49) * mm, v(-248, 277.49) * mm, v(-244.12, 273.87) * mm, v(-244.15, 270.45) * mm, v(-253.07, 273.83) * mm, v(-264.72, 272.13) * mm, v(-278.82, 270.02) * mm, v(-290.67, 270.62) * mm, v(-293.87, 274.3) * mm]});
            skFitSpline(sketch, "E63", {"points": [v(-294.8, 284.7) * mm, v(-291.14, 280.67) * mm, v(-282.77, 278.5) * mm, v(-269.52, 281.57) * mm, v(-257.7, 282.82) * mm, v(-247.2, 281.38) * mm, v(-244.65, 280.36) * mm, v(-248.26, 285.94) * mm, v(-257.8, 287.54) * mm, v(-271.17, 285.77) * mm, v(-284.3, 284.54) * mm, v(-294.8, 284.7) * mm]});
            skFitSpline(sketch, "E64", {"points": [v(-308.48, 370.22) * mm, v(-298.63, 371.88) * mm, v(-286.55, 378.07) * mm, v(-275.23, 382.67) * mm, v(-266.53, 383.04) * mm, v(-257.8, 380.2) * mm, v(-255.6, 374.73) * mm, v(-256.44, 373.64) * mm, v(-267.98, 374.25) * mm, v(-279.02, 371.84) * mm, v(-288.63, 367.91) * mm, v(-297.69, 366.07) * mm, v(-305.4, 367.15) * mm, v(-308.48, 370.22) * mm]});
            skFitSpline(sketch, "E65", {"points": [v(-308.24, 361.71) * mm, v(-301.89, 358.77) * mm, v(-293.1, 358.63) * mm, v(-283.74, 361.38) * mm, v(-272.63, 365.4) * mm, v(-263.16, 365.58) * mm, v(-256.55, 363.28) * mm, v(-254.15, 361.64) * mm, v(-255.28, 366.49) * mm, v(-262.01, 370.01) * mm, v(-274.52, 369.54) * mm, v(-286.03, 364.76) * mm, v(-295.76, 362.06) * mm, v(-308.24, 361.71) * mm]});
            skFitSpline(sketch, "E66", {"points": [v(-252.43, 354.15) * mm, v(-261.7, 359.87) * mm, v(-274.44, 360.1) * mm, v(-284.88, 355.73) * mm, v(-294.65, 353.44) * mm, v(-306.08, 354.58) * mm, v(-306.91, 351.72) * mm, v(-305.56, 349.8) * mm, v(-297.2, 349.98) * mm, v(-285.77, 351.94) * mm, v(-275.53, 354.71) * mm, v(-267.04, 355.55) * mm, v(-252.43, 354.15) * mm]});
            skFitSpline(sketch, "E67", {"points": [v(-303.3, 342.52) * mm, v(-294.6, 344.4) * mm, v(-284.38, 347.72) * mm, v(-273.48, 350.69) * mm, v(-264.18, 351.3) * mm, v(-254.15, 349.92) * mm, v(-252.35, 347.14) * mm, v(-251.3, 343.1) * mm, v(-256.17, 345.45) * mm, v(-266.68, 346.89) * mm, v(-277.4, 344.17) * mm, v(-288.88, 340.2) * mm, v(-301.4, 339.05) * mm, v(-303.3, 342.52) * mm]});
            skFitSpline(sketch, "E68", {"points": [v(-303.5, 332.57) * mm, v(-302.53, 330.05) * mm, v(-297.68, 326.9) * mm, v(-290.24, 328.28) * mm, v(-280.42, 331.15) * mm, v(-267.42, 334.69) * mm, v(-257.39, 336.12) * mm, v(-251.19, 333.35) * mm, v(-251.26, 336.88) * mm, v(-257.43, 340.7) * mm, v(-274.56, 340.62) * mm, v(-287.62, 335.47) * mm, v(-299.56, 332.85) * mm, v(-303.5, 332.57) * mm]});
            skFitSpline(sketch, "E69", {"points": [v(-300.71, 322.32) * mm, v(-289.65, 322.77) * mm, v(-280.35, 324.95) * mm, v(-269.53, 329.42) * mm, v(-261.6, 331.3) * mm, v(-253.26, 329.6) * mm, v(-248.11, 324.2) * mm, v(-248.34, 320.05) * mm, v(-250.58, 320.7) * mm, v(-256.07, 322.62) * mm, v(-266.75, 322.32) * mm, v(-276.57, 320.2) * mm, v(-288.23, 318.5) * mm, v(-297.28, 318.47) * mm, v(-300.71, 322.32) * mm]});
            skFitSpline(sketch, "E70", {"points": [v(-296.03, 313.36) * mm, v(-291.93, 309.33) * mm, v(-283.72, 308.22) * mm, v(-271.16, 310) * mm, v(-255.4, 309.4) * mm, v(-247.6, 307.58) * mm, v(-249.35, 313.31) * mm, v(-254.73, 317.5) * mm, v(-265.35, 318.81) * mm, v(-275.47, 316.06) * mm, v(-287, 314.63) * mm, v(-296.03, 313.36) * mm]});
            skFitSpline(sketch, "E71", {"points": [v(-246.88, 294.27) * mm, v(-246.98, 301.15) * mm, v(-253.6, 304) * mm, v(-261.4, 305.36) * mm, v(-278.81, 304.54) * mm, v(-290.42, 305.44) * mm, v(-294.08, 305.76) * mm, v(-291.09, 302.15) * mm, v(-285, 300.33) * mm, v(-274.5, 300.1) * mm, v(-260.47, 300.13) * mm, v(-250.05, 297.63) * mm, v(-246.88, 294.27) * mm]});
            skFitSpline(sketch, "E72", {"points": [v(-255.21, 292.34) * mm, v(-266.48, 291.84) * mm, v(-276.76, 289.48) * mm, v(-288.53, 289.58) * mm, v(-296.3, 292.3) * mm, v(-296.73, 295.71) * mm, v(-296.37, 298.1) * mm, v(-290.57, 295.5) * mm, v(-280.78, 294.82) * mm, v(-267.1, 295.56) * mm, v(-259.58, 295.3) * mm, v(-255.21, 292.34) * mm]});
            skFitSpline(sketch, "E73", {"points": [v(-201.4, -43.65) * mm, v(-189.4, -37.57) * mm, v(-174.42, -35.4) * mm, v(-164.73, -34.1) * mm, v(-154.56, -30.17) * mm, v(-139.37, -17.9) * mm, v(-134.78, -16.05) * mm, v(-135.22, -19.5) * mm, v(-139.17, -30.17) * mm, v(-151.54, -40.1) * mm, v(-164.73, -43.26) * mm, v(-177.07, -42.34) * mm, v(-190.43, -43.39) * mm, v(-201.4, -43.65) * mm]});
            skFitSpline(sketch, "E74", {"points": [v(-215.8, -51.03) * mm, v(-214.97, -41.97) * mm, v(-209.78, -33.46) * mm, v(-201.75, -26.9) * mm, v(-190.17, -22.4) * mm, v(-174.47, -20.85) * mm, v(-161.75, -18.1) * mm, v(-150, -15.24) * mm, v(-137.95, -8.38) * mm, v(-134.72, -7.16) * mm, v(-136.4, -9.38) * mm, v(-145.88, -18.18) * mm, v(-156.73, -25.19) * mm, v(-170.56, -31.02) * mm, v(-186.92, -30.9) * mm, v(-202.72, -37.83) * mm, v(-211.11, -46.22) * mm, v(-215.8, -51.03) * mm]});
            skFitSpline(sketch, "E75", {"points": [v(-215.64, -33) * mm, v(-210, -21.04) * mm, v(-198.51, -13.3) * mm, v(-180.04, -9.11) * mm, v(-162.65, -6.52) * mm, v(-144.8, -3.2) * mm, v(-134.72, 3.98) * mm, v(-135.85, 0) * mm, v(-143.56, -7.16) * mm, v(-156.52, -12.44) * mm, v(-174.15, -14.93) * mm, v(-191.31, -17.48) * mm, v(-204.22, -22.17) * mm, v(-215.64, -33) * mm]});
            skFitSpline(sketch, "E76", {"points": [v(-213.8, -16.9) * mm, v(-210.63, -9.44) * mm, v(-202.68, -3.17) * mm, v(-191.9, 0) * mm, v(-176.57, 0) * mm, v(-172.28, 2.52) * mm, v(-160.14, 3.29) * mm, v(-146.86, 7.7) * mm, v(-133.5, 16.63) * mm, v(-131.43, 17.88) * mm, v(-131.7, 15.8) * mm, v(-135.07, 8.8) * mm, v(-147.26, 1.55) * mm, v(-161.86, -3.15) * mm, v(-179.57, -4.6) * mm, v(-192.54, -6.77) * mm, v(-203.18, -10.45) * mm, v(-209.46, -14.66) * mm, v(-211.99, -17.52) * mm, v(-213.75, -18.66) * mm, v(-213.8, -16.9) * mm]});
            skFitSpline(sketch, "E77", {"points": [v(-241.26, 397.9) * mm, v(-232.83, 403.14) * mm, v(-228.78, 406.64) * mm, v(-225, 405.42) * mm, v(-222.9, 400.97) * mm, v(-230.9, 397) * mm, v(-241.15, 389.7) * mm, v(-249.65, 386.74) * mm, v(-252.2, 386.3) * mm, v(-251.7, 389.66) * mm, v(-251.55, 392.12) * mm, v(-246.59, 393.22) * mm, v(-241.26, 397.9) * mm]});
            skFitSpline(sketch, "E78", {"points": [v(-248.7, 380.15) * mm, v(-242.8, 384.18) * mm, v(-238.14, 385.51) * mm, v(-229.24, 392.22) * mm, v(-223.1, 395.66) * mm, v(-215.83, 395.14) * mm, v(-215.74, 390.37) * mm, v(-224.6, 384.8) * mm, v(-236.05, 381.07) * mm, v(-243.1, 378.32) * mm, v(-247.48, 373.14) * mm, v(-249.6, 373.98) * mm, v(-249.98, 377.26) * mm, v(-248.7, 380.15) * mm]});
            skFitSpline(sketch, "E79", {"points": [v(-245.44, 362.28) * mm, v(-246.23, 369.34) * mm, v(-242.52, 371.28) * mm, v(-239.91, 374.32) * mm, v(-230.7, 377.26) * mm, v(-223.73, 380) * mm, v(-218.56, 381.52) * mm, v(-214.6, 385.83) * mm, v(-209.18, 386.36) * mm, v(-209.96, 383.58) * mm, v(-217.68, 377.1) * mm, v(-228.4, 374.34) * mm, v(-238.6, 369.84) * mm, v(-243.52, 364.72) * mm, v(-245.44, 362.28) * mm]});
            skFitSpline(sketch, "E80", {"points": [v(-243.46, 355.73) * mm, v(-238.08, 363.83) * mm, v(-225.12, 369.5) * mm, v(-211.38, 374.34) * mm, v(-204.39, 378.49) * mm, v(-204.64, 374.34) * mm, v(-208.3, 370.85) * mm, v(-217.14, 367.02) * mm, v(-225.91, 365.54) * mm, v(-234.06, 360.34) * mm, v(-239.8, 351.8) * mm, v(-242.22, 349.17) * mm, v(-243.55, 351.8) * mm, v(-243.46, 355.73) * mm]});
            skFitSpline(sketch, "E81", {"points": [v(-239.9, 345.03) * mm, v(-233.82, 353.69) * mm, v(-224.58, 360.46) * mm, v(-214.98, 363.12) * mm, v(-206.96, 367.69) * mm, v(-201.67, 370.46) * mm, v(-198.28, 370.68) * mm, v(-199.31, 366.53) * mm, v(-206.78, 362.75) * mm, v(-216.33, 358.37) * mm, v(-227.07, 352) * mm, v(-235.21, 346.8) * mm, v(-239.03, 339.58) * mm, v(-239.96, 341.83) * mm, v(-239.9, 345.03) * mm]});
            skFitSpline(sketch, "E82", {"points": [v(-236.26, 329.16) * mm, v(-238.63, 328.37) * mm, v(-239.4, 332.19) * mm, v(-236.3, 335.53) * mm, v(-231.3, 340.55) * mm, v(-227.26, 345.8) * mm, v(-222.56, 349.9) * mm, v(-216.23, 352.25) * mm, v(-209.89, 354.75) * mm, v(-201.84, 357.46) * mm, v(-195.52, 358.82) * mm, v(-197.82, 355.25) * mm, v(-208.8, 349.05) * mm, v(-219.93, 343.43) * mm, v(-228.98, 335.7) * mm, v(-234.95, 330.87) * mm, v(-236.26, 329.16) * mm]});
            skFitSpline(sketch, "E83", {"points": [v(-214.6, -4.6) * mm, v(-213.65, 1.62) * mm, v(-211.44, 5.88) * mm, v(-205.9, 10.06) * mm, v(-200.6, 11) * mm, v(-189.41, 11.09) * mm, v(-174.33, 14.43) * mm, v(-159.85, 20) * mm, v(-145.8, 23.94) * mm, v(-134.19, 32.2) * mm, v(-128.94, 36.13) * mm, v(-129.84, 32.2) * mm, v(-133.36, 25.57) * mm, v(-139.44, 17.72) * mm, v(-148.57, 12.27) * mm, v(-162.34, 7.7) * mm, v(-178.3, 6.66) * mm, v(-196.8, 3.96) * mm, v(-205.23, 1.49) * mm, v(-209.75, -1.8) * mm, v(-213.27, -6.8) * mm, v(-214.6, -4.6) * mm]});
            skFitSpline(sketch, "E84", {"points": [v(-212.34, 12.2) * mm, v(-211.86, 16.93) * mm, v(-205.86, 22.29) * mm, v(-195.65, 24.65) * mm, v(-180, 25.67) * mm, v(-166.88, 28.9) * mm, v(-154.34, 32.79) * mm, v(-136.66, 41.65) * mm, v(-128.91, 48.31) * mm, v(-128.67, 45.62) * mm, v(-137.28, 33.82) * mm, v(-157.63, 24.72) * mm, v(-174.52, 18.9) * mm, v(-183.48, 15.81) * mm, v(-197.22, 16.84) * mm, v(-207.74, 15.19) * mm, v(-212.21, 11.26) * mm, v(-212.34, 12.2) * mm]});
            skFitSpline(sketch, "E85", {"points": [v(-211.76, 24.23) * mm, v(-201.64, 28.23) * mm, v(-185.08, 30.36) * mm, v(-166.38, 33.84) * mm, v(-147.15, 39.96) * mm, v(-132.74, 51.1) * mm, v(-127.22, 58.78) * mm, v(-128.32, 59.45) * mm, v(-132.9, 55.84) * mm, v(-150.73, 47.4) * mm, v(-164.5, 42.5) * mm, v(-180.91, 41.16) * mm, v(-196.72, 39.07) * mm, v(-205.43, 34.09) * mm, v(-210, 28.6) * mm, v(-211.76, 24.23) * mm]});
            skFitSpline(sketch, "E86", {"points": [v(-211.9, 34.61) * mm, v(-212.24, 38.43) * mm, v(-210.22, 41.68) * mm, v(-200.34, 48.81) * mm, v(-183.2, 52.62) * mm, v(-153.7, 59.76) * mm, v(-136.2, 65.94) * mm, v(-126.06, 71.3) * mm, v(-128.98, 66.67) * mm, v(-138.24, 57.04) * mm, v(-157.56, 48.65) * mm, v(-176.2, 45.43) * mm, v(-191.06, 43.76) * mm, v(-199.86, 43.23) * mm, v(-206.03, 38.47) * mm, v(-211.9, 34.61) * mm]});
            skFitSpline(sketch, "E87", {"points": [v(-211.7, 46.71) * mm, v(-212.3, 49.88) * mm, v(-207.81, 54.85) * mm, v(-196.44, 60.18) * mm, v(-179.28, 62.78) * mm, v(-160.03, 70.23) * mm, v(-141.94, 78.1) * mm, v(-128.8, 85.37) * mm, v(-125.23, 87.08) * mm, v(-125.82, 81.1) * mm, v(-133.96, 72.13) * mm, v(-162.05, 61.46) * mm, v(-191.22, 54.69) * mm, v(-206.85, 48.81) * mm, v(-211.5, 44.53) * mm, v(-211.7, 46.71) * mm]});
            skFitSpline(sketch, "E88", {"points": [v(-212.46, 60.14) * mm, v(-203.82, 68.5) * mm, v(-187.7, 77.69) * mm, v(-160.32, 86.03) * mm, v(-143.69, 93.4) * mm, v(-126.75, 104.78) * mm, v(-124.76, 104.8) * mm, v(-125.72, 96.98) * mm, v(-131, 89.82) * mm, v(-153.22, 78.15) * mm, v(-181.33, 69.23) * mm, v(-198.15, 65.24) * mm, v(-211.06, 57.81) * mm, v(-212.46, 60.14) * mm]});
            skFitSpline(sketch, "E89", {"points": [v(-235.75, 311.66) * mm, v(-236.2, 317.76) * mm, v(-235.3, 320.83) * mm, v(-230.59, 326.9) * mm, v(-219.06, 338.47) * mm, v(-208.37, 343.8) * mm, v(-198.17, 347.39) * mm, v(-190.83, 348.6) * mm, v(-194.71, 345.9) * mm, v(-201.94, 340.44) * mm, v(-216.23, 334.38) * mm, v(-222.9, 325.71) * mm, v(-225.84, 319.36) * mm, v(-235.75, 311.66) * mm]});
            skFitSpline(sketch, "E90", {"points": [v(-233.79, 306.88) * mm, v(-223.56, 315.45) * mm, v(-218.16, 324.3) * mm, v(-211.47, 329.83) * mm, v(-199.25, 337.24) * mm, v(-191.03, 340) * mm, v(-186.98, 340.71) * mm, v(-187.64, 337.47) * mm, v(-190.95, 333.5) * mm, v(-201.1, 328.1) * mm, v(-211.77, 318.68) * mm, v(-221.88, 307.23) * mm, v(-226.1, 305.63) * mm, v(-231.57, 299.96) * mm, v(-233.65, 300.67) * mm, v(-233.79, 306.88) * mm]});
            skFitSpline(sketch, "E91", {"points": [v(-231.13, 289.08) * mm, v(-231.2, 293.63) * mm, v(-228.12, 297.78) * mm, v(-219.5, 303.26) * mm, v(-211.61, 309.2) * mm, v(-205.77, 316.04) * mm, v(-197.43, 324.23) * mm, v(-190.36, 326.83) * mm, v(-186.13, 327.07) * mm, v(-184.07, 329.16) * mm, v(-183.08, 322.16) * mm, v(-188.95, 315.17) * mm, v(-200.63, 309.05) * mm, v(-207.95, 306.63) * mm, v(-217.05, 300.2) * mm, v(-228.4, 290.86) * mm, v(-231.13, 289.08) * mm]});
            skFitSpline(sketch, "E92", {"points": [v(-229.82, 282) * mm, v(-221.72, 290.36) * mm, v(-208.87, 298.13) * mm, v(-198.54, 303.34) * mm, v(-191.77, 307.3) * mm, v(-183.92, 313.3) * mm, v(-176.98, 314.83) * mm, v(-177.96, 307.76) * mm, v(-185.6, 301.74) * mm, v(-202.11, 296.58) * mm, v(-214.1, 290.86) * mm, v(-229.82, 282) * mm]});
            skFitSpline(sketch, "E93", {"points": [v(-228.33, 269.89) * mm, v(-226.15, 277.5) * mm, v(-220.2, 283.2) * mm, v(-208.66, 289.62) * mm, v(-186.02, 297.53) * mm, v(-174.18, 303.16) * mm, v(-174.82, 296.27) * mm, v(-184.57, 291.46) * mm, v(-199.15, 286.14) * mm, v(-217.34, 278.13) * mm, v(-224.86, 270.6) * mm, v(-228.33, 269.89) * mm]});
            skFitSpline(sketch, "E94", {"points": [v(-212.4, 68.54) * mm, v(-208.04, 77.69) * mm, v(-198.4, 83.44) * mm, v(-179.47, 90.93) * mm, v(-158.84, 99.27) * mm, v(-141.22, 109.94) * mm, v(-129.07, 119.78) * mm, v(-126.48, 123.64) * mm, v(-126.48, 117.99) * mm, v(-128.87, 109.02) * mm, v(-141.13, 99.35) * mm, v(-176.18, 85.84) * mm, v(-194.83, 79.68) * mm, v(-202.85, 74.47) * mm, v(-212.4, 68.54) * mm]});
            skFitSpline(sketch, "E95", {"points": [v(-212.4, 80.33) * mm, v(-213.34, 87.4) * mm, v(-206.58, 93.97) * mm, v(-184.4, 100.3) * mm, v(-163.82, 107.74) * mm, v(-136.3, 122.64) * mm, v(-129.3, 128.28) * mm, v(-137.06, 117.44) * mm, v(-163.9, 99.74) * mm, v(-192.26, 91.75) * mm, v(-205.61, 84.94) * mm, v(-210.84, 79.08) * mm, v(-212.4, 80.33) * mm]});
            skFitSpline(sketch, "E96", {"points": [v(-213.15, 93.97) * mm, v(-211, 104.19) * mm, v(-199.54, 112.96) * mm, v(-178.95, 118.9) * mm, v(-146.28, 130.48) * mm, v(-130.05, 142.73) * mm, v(-127.82, 144.49) * mm, v(-127.23, 139.66) * mm, v(-136.3, 128.28) * mm, v(-161.61, 113.48) * mm, v(-187.36, 105.1) * mm, v(-206.58, 100.22) * mm, v(-213.15, 93.97) * mm]});
            skFitSpline(sketch, "E97", {"points": [v(-213.73, 110.64) * mm, v(-207.45, 120.28) * mm, v(-193.73, 128.3) * mm, v(-172.28, 132.92) * mm, v(-145.3, 144.15) * mm, v(-130.21, 151.13) * mm, v(-130.15, 148.84) * mm, v(-139.06, 140.52) * mm, v(-162.22, 127.4) * mm, v(-181.26, 123.61) * mm, v(-204.2, 114.89) * mm, v(-214.3, 109.14) * mm, v(-213.73, 110.64) * mm]});
            skFitSpline(sketch, "E98", {"points": [v(-214.12, 118.86) * mm, v(-213.99, 123.61) * mm, v(-204.2, 134.3) * mm, v(-192.3, 139.98) * mm, v(-177.37, 144.42) * mm, v(-157.03, 149.53) * mm, v(-142.47, 153.83) * mm, v(-131.05, 161.75) * mm, v(-129.76, 158.55) * mm, v(-135.98, 152.08) * mm, v(-159.73, 142.25) * mm, v(-188.01, 134.3) * mm, v(-201.43, 130.44) * mm, v(-209.83, 123.61) * mm, v(-214.12, 118.86) * mm]});
            skFitSpline(sketch, "E99", {"points": [v(-215.08, 133.53) * mm, v(-208.3, 144.66) * mm, v(-192.83, 153.02) * mm, v(-174.41, 155.45) * mm, v(-152.07, 161.67) * mm, v(-133.44, 171.98) * mm, v(-131.24, 170.21) * mm, v(-133.34, 164.7) * mm, v(-154.53, 153.42) * mm, v(-184, 147) * mm, v(-204.2, 139.11) * mm, v(-213.47, 130.76) * mm, v(-215.08, 133.53) * mm]});
            skFitSpline(sketch, "E100", {"points": [v(-215.74, 151.85) * mm, v(-209.03, 159.01) * mm, v(-191.9, 165.74) * mm, v(-172.33, 170.18) * mm, v(-146.68, 178.71) * mm, v(-133.92, 184.56) * mm, v(-134.4, 180.9) * mm, v(-139.76, 173.86) * mm, v(-157.46, 164.35) * mm, v(-179.7, 159.67) * mm, v(-198.34, 155.98) * mm, v(-211.63, 148.77) * mm, v(-214.86, 143.18) * mm, v(-215.74, 151.85) * mm]});
            skFitSpline(sketch, "E101", {"points": [v(-216.86, 163.57) * mm, v(-210.37, 170.13) * mm, v(-197.1, 175.87) * mm, v(-183.49, 178.99) * mm, v(-167.02, 180.16) * mm, v(-151.89, 185.66) * mm, v(-139.4, 191.97) * mm, v(-135.61, 193.9) * mm, v(-137.42, 189.32) * mm, v(-152.67, 181.75) * mm, v(-163.77, 175.75) * mm, v(-188.07, 170.9) * mm, v(-207.46, 166.25) * mm, v(-216.01, 158.98) * mm, v(-216.86, 163.57) * mm]});
            skFitSpline(sketch, "E102", {"points": [v(-226.89, 256.59) * mm, v(-227.4, 260.82) * mm, v(-227.46, 264.2) * mm, v(-224.44, 267.46) * mm, v(-216.83, 272.58) * mm, v(-206.25, 278.28) * mm, v(-196.57, 282.6) * mm, v(-185.8, 287.34) * mm, v(-175.44, 291.99) * mm, v(-171.72, 295.03) * mm, v(-170.87, 290.61) * mm, v(-174.65, 285.42) * mm, v(-184.75, 279.67) * mm, v(-200.36, 273.65) * mm, v(-212.06, 269.17) * mm, v(-219.87, 263.67) * mm, v(-225.05, 257.7) * mm, v(-226.89, 256.59) * mm]});
            skFitSpline(sketch, "E103", {"points": [v(-225.57, 248.34) * mm, v(-220.64, 257.43) * mm, v(-206.7, 266.21) * mm, v(-188.59, 272.33) * mm, v(-174.75, 278.16) * mm, v(-167.5, 284) * mm, v(-166.3, 285.6) * mm, v(-165.74, 282.84) * mm, v(-167.3, 276.3) * mm, v(-183.6, 264.44) * mm, v(-210.07, 255.05) * mm, v(-219.17, 249.3) * mm, v(-225.19, 245.33) * mm, v(-225.57, 248.34) * mm]});
            skFitSpline(sketch, "E104", {"points": [v(-217.6, 170.67) * mm, v(-217.52, 175.16) * mm, v(-211.79, 180.56) * mm, v(-201.08, 185.18) * mm, v(-186.3, 186.23) * mm, v(-171.3, 189.05) * mm, v(-153.5, 194.4) * mm, v(-138.34, 207.1) * mm, v(-136.57, 208.5) * mm, v(-137.8, 203.25) * mm, v(-140.63, 196.6) * mm, v(-153.7, 188.5) * mm, v(-174.33, 184.75) * mm, v(-191.5, 182.56) * mm, v(-206.63, 177.41) * mm, v(-217.6, 170.67) * mm]});
            skFitSpline(sketch, "E105", {"points": [v(-223.06, 231.5) * mm, v(-224.25, 235.5) * mm, v(-221.47, 241.63) * mm, v(-214.98, 246.35) * mm, v(-199.83, 252.4) * mm, v(-182.12, 259.09) * mm, v(-167.86, 268.37) * mm, v(-163.66, 273.85) * mm, v(-161.33, 273.32) * mm, v(-162.18, 266.94) * mm, v(-168.83, 256.97) * mm, v(-186.45, 248.58) * mm, v(-202.09, 244.51) * mm, v(-215.13, 237.96) * mm, v(-223.06, 231.5) * mm]});
            skFitSpline(sketch, "E106", {"points": [v(-221.18, 217.83) * mm, v(-221.77, 223.67) * mm, v(-218, 229.2) * mm, v(-211.81, 234.67) * mm, v(-202.45, 238.32) * mm, v(-188.51, 241.64) * mm, v(-172.8, 250.5) * mm, v(-162.72, 257.65) * mm, v(-157.04, 263.91) * mm, v(-157.17, 261.05) * mm, v(-159.86, 253.22) * mm, v(-177.96, 239.14) * mm, v(-196.44, 230.86) * mm, v(-212, 223.9) * mm, v(-221.18, 217.83) * mm]});
            skFitSpline(sketch, "E107", {"points": [v(-221.2, 207.25) * mm, v(-221.75, 211.1) * mm, v(-216.34, 216.54) * mm, v(-204.67, 222.65) * mm, v(-176.91, 233.79) * mm, v(-166.27, 242.18) * mm, v(-154.03, 253.62) * mm, v(-152.66, 252.19) * mm, v(-153.79, 244.96) * mm, v(-172.4, 230.71) * mm, v(-197.2, 221.9) * mm, v(-214.8, 213.48) * mm, v(-221.2, 207.25) * mm]});
            skFitSpline(sketch, "E108", {"points": [v(-218.14, 185.16) * mm, v(-208.19, 192.8) * mm, v(-188.97, 201.48) * mm, v(-171.15, 204.32) * mm, v(-151.65, 208.87) * mm, v(-141.5, 218.65) * mm, v(-141.25, 209.99) * mm, v(-153.3, 200.67) * mm, v(-172.87, 194.69) * mm, v(-194.79, 192.36) * mm, v(-206.9, 187.13) * mm, v(-217.19, 180) * mm, v(-218.14, 185.16) * mm]});
            skFitSpline(sketch, "E109", {"points": [v(-216.96, 190.94) * mm, v(-219.4, 192.99) * mm, v(-212.15, 198.83) * mm, v(-199.16, 207.19) * mm, v(-184.22, 212.35) * mm, v(-167.2, 215.5) * mm, v(-153.72, 220.84) * mm, v(-146.45, 229.77) * mm, v(-144.9, 225.14) * mm, v(-143.86, 221.1) * mm, v(-153.53, 214.35) * mm, v(-171.06, 208.7) * mm, v(-185.64, 205.92) * mm, v(-199.58, 201.45) * mm, v(-216.96, 190.94) * mm]});
            skFitSpline(sketch, "E110", {"points": [v(-220.82, 199.5) * mm, v(-211.94, 209.7) * mm, v(-197.8, 216.99) * mm, v(-182.9, 222.56) * mm, v(-164.4, 229.97) * mm, v(-149.89, 241.65) * mm, v(-149.75, 236.78) * mm, v(-151.2, 229.01) * mm, v(-163.13, 222.14) * mm, v(-182.44, 218.73) * mm, v(-206.52, 208.23) * mm, v(-218.8, 198.44) * mm, v(-220.82, 199.5) * mm]});
            skSolve(sketch);
        }
        {
            var Q0;
            Q0 = qSketchRegion(id + "F0", true);
            extrude(context, id + "F1", {"entities" : qUnion([Q0]), "depth" : 3.17 * mm});
        }
    });
